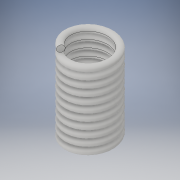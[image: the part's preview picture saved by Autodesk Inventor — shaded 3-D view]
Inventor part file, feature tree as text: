
AUTODESK INVENTOR PART (.ipt)
format: ipt  version: 2018 (Build 220112000, 112)  size: 499,712 bytes
history: native  units: in
note: dims shown in document units (in); Inventor stores cm internally (conversion verified against a paired STEP export)
features: helix x1, sketch x1
ambient origin geometry x8: Origin, YZ Plane, XZ Plane, XY Plane, X Axis, Y Axis, Z Axis, Center Point
bodies: Solid1 (feature_tree)
feature tree (2):
  helix  "Coil1"  [1 undecoded]
  sketch  "Sketch1"  dims[d1=0.077in d2=1.0in d3=0.2479in d4=4.3307in d5=0.0in d6=30.0deg d7=0.0in d8=30.0deg d9=0.0in]
note: 1 required parameter value undecoded (feature->parameter linkage not recoverable at this tier; creation-order binding heuristic only, values carry confidence <= 0.55)
